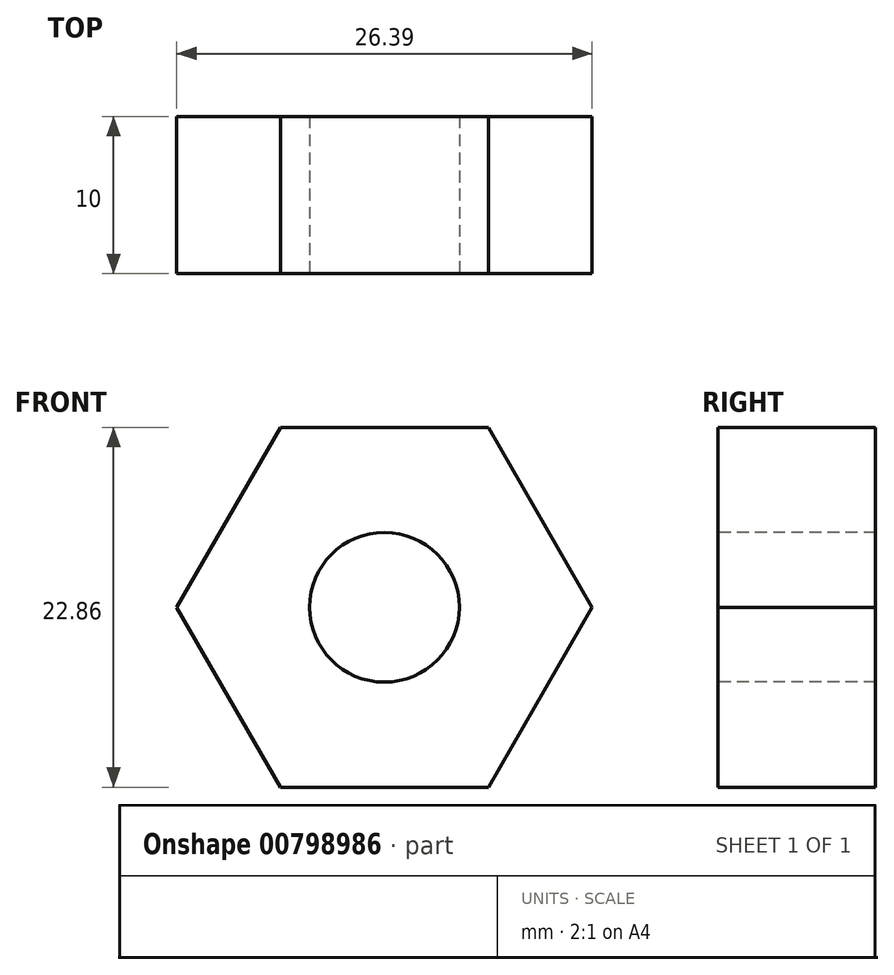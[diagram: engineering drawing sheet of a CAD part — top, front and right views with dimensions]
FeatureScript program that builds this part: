
annotation { "Feature Type Name" : "Feature", "Feature Type Description" : "" }
export const myFeature = defineFeature(function(context is Context, id is Id, definition is map)
    precondition{}
    {
        {
            var Q0;
            Q0=qCreatedBy(makeId("Front.planeOp"),FACE);
            var sketch = newSketch(context, id + "F0", { "sketchPlane" : qUnion([Q0])});
            skCircle(sketch, "E0.cCircle", {"center": v(-22.03, 14.7) * mm, "radius": 11.43 * mm, "construction": true});
            skLineSegment(sketch, "E0.0", {"start": v(-15.43, 3.27) * mm, "end": v(-28.62, 3.27) * mm});
            skLineSegment(sketch, "E0.1", {"start": v(-28.62, 3.27) * mm, "end": v(-35.22, 14.7) * mm});
            skLineSegment(sketch, "E0.2", {"start": v(-35.22, 14.7) * mm, "end": v(-28.62, 26.13) * mm});
            skLineSegment(sketch, "E0.3", {"start": v(-28.62, 26.13) * mm, "end": v(-15.43, 26.13) * mm});
            skLineSegment(sketch, "E0.4", {"start": v(-15.43, 26.13) * mm, "end": v(-8.83, 14.7) * mm});
            skLineSegment(sketch, "E0.5", {"start": v(-8.83, 14.7) * mm, "end": v(-15.43, 3.27) * mm});
            skPoint(sketch, "E0.0.midPoint", {"position": v(-22.03, 3.27) * mm});
            skCircle(sketch, "E1", {"center": v(-22.03, 14.7) * mm, "radius": 4.76 * mm});
            skSolve(sketch);
        }
        {
            var Q0;
            Q0=sQuery(id+"F0.wireOp",EDGE,"E1");
            var Q1;
            Q1=sQuery(id+"F0.wireOp",EDGE,"E0.3");
            var Q2;
            Q2=sQuery(id+"F0.wireOp",EDGE,"E0.4");
            var Q3;
            Q3=sQuery(id+"F0.wireOp",EDGE,"E0.5");
            var Q4;
            Q4=sQuery(id+"F0.wireOp",EDGE,"E0.0");
            var Q5;
            Q5=sQuery(id+"F0.wireOp",EDGE,"E0.1");
            var Q6;
            Q6=sQuery(id+"F0.wireOp",EDGE,"E0.2");
            extrude(context, id + "F1", {"bodyType" : ToolBodyType.SURFACE, "surfaceEntities" : qUnion([Q0, Q1, Q2, Q3, Q4, Q5, Q6]), "depth" : 10 * mm, "offsetDistance" : 25 * mm});
        }
    });
